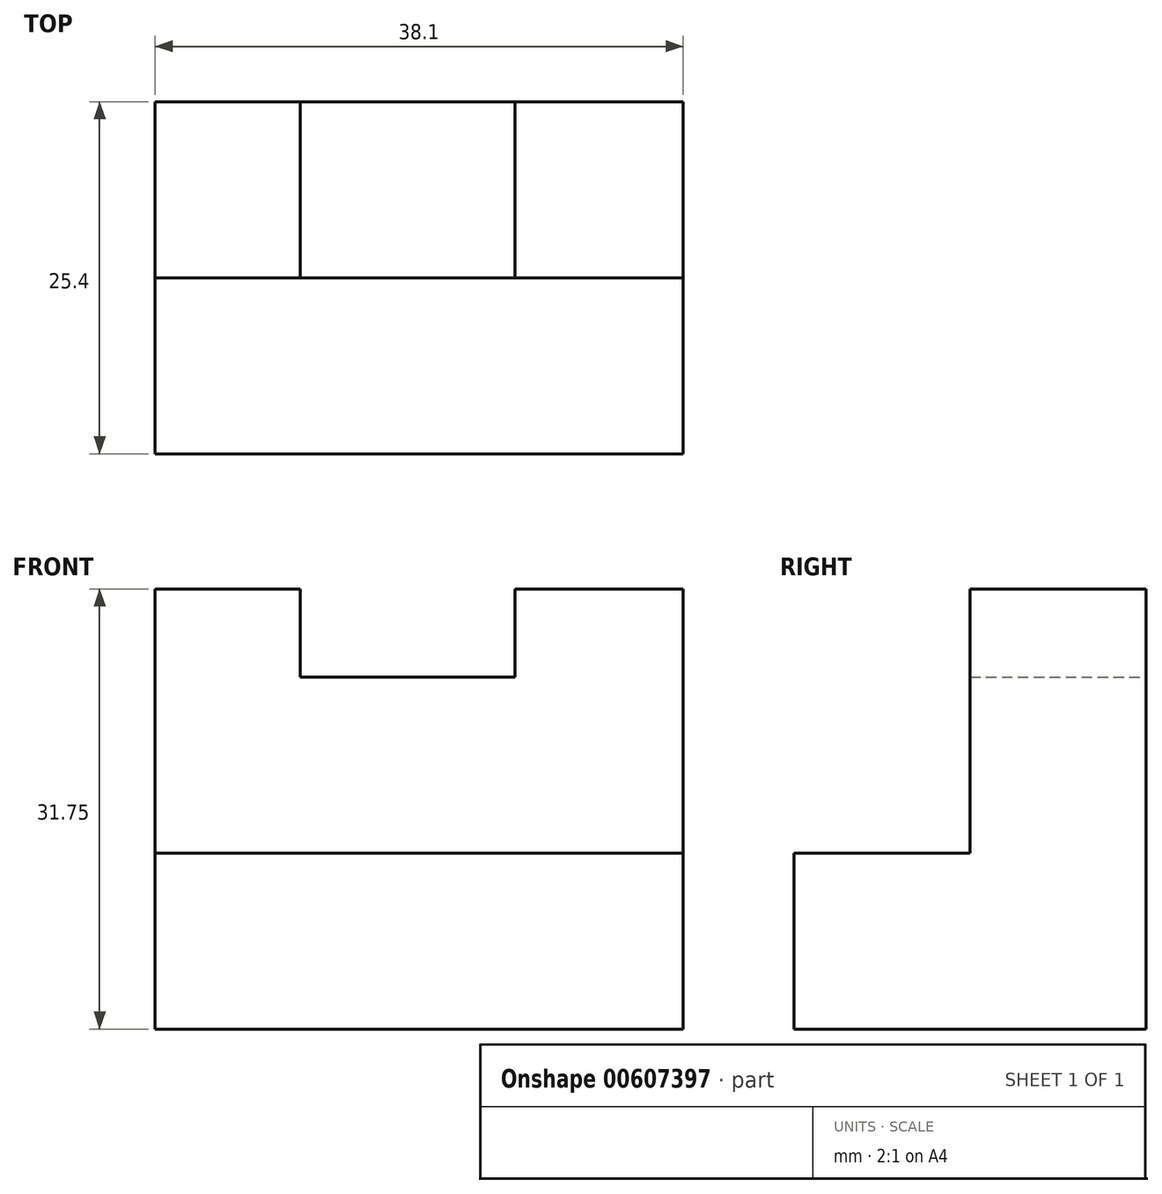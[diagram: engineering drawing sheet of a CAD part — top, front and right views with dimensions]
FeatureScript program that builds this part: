
annotation { "Feature Type Name" : "Feature", "Feature Type Description" : "" }
export const myFeature = defineFeature(function(context is Context, id is Id, definition is map)
    precondition{}
    {
        {
            var Q0;
            Q0=qCreatedBy(makeId("Right.planeOp"),FACE);
            var sketch = newSketch(context, id + "F0", { "sketchPlane" : qUnion([Q0])});
            skLineSegment(sketch, "E0", {"start": v(0, 0) * mm, "end": v(0, 31.75) * mm});
            skLineSegment(sketch, "E1", {"start": v(0, 0) * mm, "end": v(-25.4, 0) * mm});
            skLineSegment(sketch, "E2", {"start": v(-25.4, 0) * mm, "end": v(-25.4, 12.7) * mm});
            skLineSegment(sketch, "E3", {"start": v(-25.4, 12.7) * mm, "end": v(-12.7, 12.7) * mm});
            skLineSegment(sketch, "E4", {"start": v(-12.7, 12.7) * mm, "end": v(-12.7, 31.75) * mm});
            skLineSegment(sketch, "E5", {"start": v(-12.7, 31.75) * mm, "end": v(0, 31.75) * mm});
            skSolve(sketch);
        }
        {
            var Q0;
            Q0=makeQuery(id+"F0.imprint","IMPRINT",FACE,{"disambiguationData":[TD([[makeQuery(id+"F0.imprint","IMPRINT",EDGE,{"derivedFrom":sQuery(id+"F0.wireOp",EDGE,"E0")}),1.0]])]});
            extrude(context, id + "F1", {"entities" : qUnion([Q0]), "depth" : 25.4 * mm, "offsetDistance" : 25.4 * mm});
        }
        {
            var Q0;
            Q0=makeQuery(id+"F1.opExtrude","CAP_FACE",FACE,{"disambiguationData":[OSD([sQuery(id+"F0.wireOp",EDGE,"E0"),sQuery(id+"F0.wireOp",EDGE,"E1"),sQuery(id+"F0.wireOp",EDGE,"E2"),sQuery(id+"F0.wireOp",EDGE,"E3"),sQuery(id+"F0.wireOp",EDGE,"E4"),sQuery(id+"F0.wireOp",EDGE,"E5")])],"isStart":false});
            extrude(context, id + "F2", {"entities" : qUnion([Q0]), "operationType" : NewBodyOperationType.ADD, "depth" : 12.7 * mm, "offsetDistance" : 25.4 * mm});
        }
        {
            var Q0;
            {var subQ0=sQuery(id+"F0.wireOp",EDGE,"E5");Q0=makeQuery(id+"F2.boolean.opBoolean","MERGE",FACE,{"derivedFrom":[makeQuery(id+"F1.opExtrude","SWEPT_FACE",FACE,{"disambiguationData":[OSD([subQ0])]}),makeQuery(id+"F2.opExtrude","SWEPT_FACE",FACE,{"disambiguationData":[OSD([subQ0])]})]});}
            var sketch = newSketch(context, id + "F3", { "sketchPlane" : qUnion([Q0])});
            skLineSegment(sketch, "E6", {"start": v(10.46, -12.7) * mm, "end": v(10.46, 0) * mm});
            skLineSegment(sketch, "E7", {"start": v(25.95, -12.7) * mm, "end": v(25.95, 0) * mm});
            skLineSegment(sketch, "E8", {"start": v(10.46, -12.7) * mm, "end": v(25.95, -12.7) * mm});
            skLineSegment(sketch, "E9", {"start": v(25.95, 0) * mm, "end": v(10.46, 0) * mm});
            skSolve(sketch);
        }
        {
            var Q0;
            Q0=makeQuery(id+"F3.imprint","IMPRINT",FACE,{"disambiguationData":[TD([[makeQuery(id+"F3.imprint","IMPRINT",EDGE,{"derivedFrom":sQuery(id+"F3.wireOp",EDGE,"E6")}),-1.0]])]});
            extrude(context, id + "F4", {"entities" : qUnion([Q0]), "operationType" : NewBodyOperationType.REMOVE, "oppositeDirection" : true, "depth" : 6.35 * mm, "offsetDistance" : 25.4 * mm});
        }
    });
